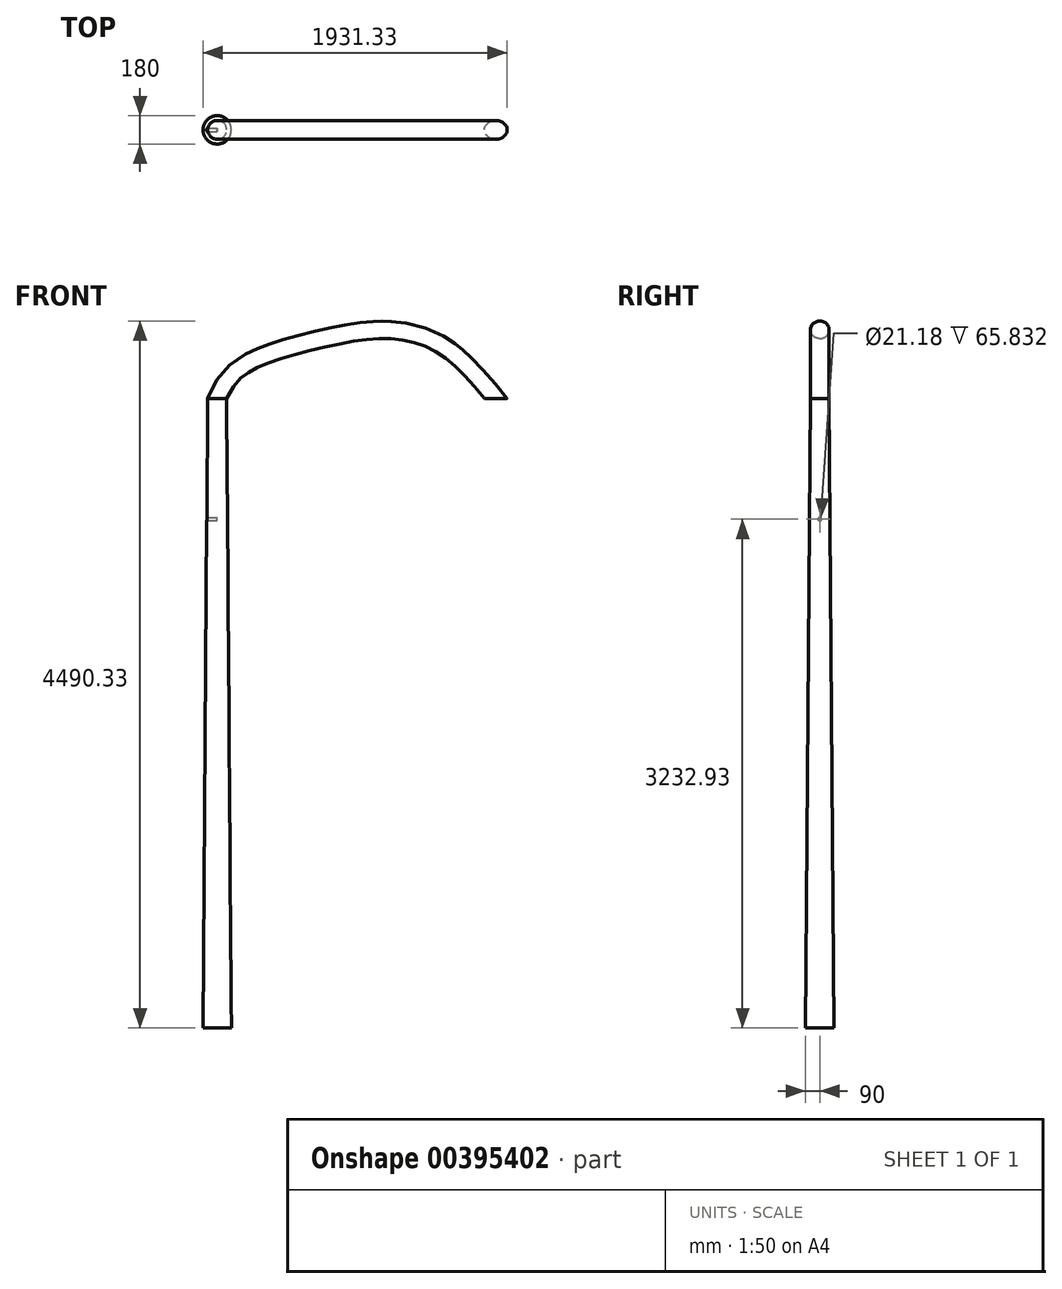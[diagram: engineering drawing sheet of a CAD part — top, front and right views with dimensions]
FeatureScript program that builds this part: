
annotation { "Feature Type Name" : "Feature", "Feature Type Description" : "" }
export const myFeature = defineFeature(function(context is Context, id is Id, definition is map)
    precondition{}
    {
        {
            var Q0;
            Q0=qCreatedBy(makeId("Top.planeOp"),FACE);
            var sketch = newSketch(context, id + "F0", { "sketchPlane" : qUnion([Q0])});
            skCircle(sketch, "E0", {"center": v(0, 0) * mm, "radius": 60 * mm});
            skSolve(sketch);
        }
        {
            var Q0;
            Q0=qCreatedBy(makeId("Top.planeOp"),FACE);
            cPlane(context, id + "F1", {"entities" : qUnion([Q0]), "cplaneType" : CPlaneType.OFFSET, "offset" : 4000 * mm, "oppositeDirection" : true, "width" : 150 * mm, "height" : 150 * mm});
        }
        {
            var Q0;
            Q0=qCreatedBy(id+"F1.planeOp",FACE);
            var sketch = newSketch(context, id + "F2", { "sketchPlane" : qUnion([Q0])});
            skCircle(sketch, "E1", {"center": v(0, 0) * mm, "radius": 90 * mm});
            skSolve(sketch);
        }
        {
            var Q0;
            Q0=makeQuery(id+"F0.imprint","IMPRINT",FACE,{"disambiguationData":[TD([[makeQuery(id+"F0.imprint","IMPRINT",EDGE,{"derivedFrom":sQuery(id+"F0.wireOp",EDGE,"E0")}),1.0]])]});
            var Q1;
            Q1=makeQuery(id+"F2.imprint","IMPRINT",FACE,{"disambiguationData":[TD([[makeQuery(id+"F2.imprint","IMPRINT",EDGE,{"derivedFrom":sQuery(id+"F2.wireOp",EDGE,"E1")}),1.0]])]});
            loft(context, id + "F3", {"sheetProfilesArray" : [{ "sheetProfileEntities" : qUnion([Q0]) }, { "sheetProfileEntities" : qUnion([Q1]) }]});
        }
        {
            var Q0;
            Q0=qCreatedBy(makeId("Right.planeOp"),FACE);
            cPlane(context, id + "F4", {"entities" : qUnion([Q0]), "cplaneType" : CPlaneType.OFFSET, "offset" : 1100 * mm, "width" : 150 * mm, "height" : 150 * mm});
        }
        {
            var Q0;
            Q0=qCreatedBy(id+"F4.planeOp",FACE);
            var sketch = newSketch(context, id + "F5", { "sketchPlane" : qUnion([Q0])});
            skCircle(sketch, "E2", {"center": v(0, 405) * mm, "radius": 84.19 * mm});
            skSolve(sketch);
        }
        {
            var Q0;
            Q0=qCreatedBy(makeId("Top.planeOp"),FACE);
            var sketch = newSketch(context, id + "F6", { "sketchPlane" : qUnion([Q0])});
            skCircle(sketch, "E3", {"center": v(1778.5, 0) * mm, "radius": 62.82 * mm});
            skSolve(sketch);
        }
        {
            var Q0;
            Q0=qCreatedBy(makeId("Front.planeOp"),FACE);
            var sketch = newSketch(context, id + "F7", { "sketchPlane" : qUnion([Q0])});
            skLineSegment(sketch, "E4.0", {"start": v(1100, 489.2) * mm, "end": v(1100, 320.82) * mm});
            skLineSegment(sketch, "E5.0", {"start": v(60, 0) * mm, "end": v(-60, 0) * mm});
            skLineSegment(sketch, "E6", {"start": v(1100, 405) * mm, "end": v(1100, 489.2) * mm});
            skLineSegment(sketch, "E7", {"start": v(30, 0) * mm, "end": v(-60, 0) * mm});
            skLineSegment(sketch, "E8.0", {"start": v(1715.69, 0) * mm, "end": v(1841.33, 0) * mm});
            skFitSpline(sketch, "E9", {"points": [v(-60, 0) * mm, v(204.15, 292.84) * mm, v(690.76, 441.3) * mm, v(1100, 489.2) * mm, v(1475.98, 372.42) * mm, v(1841.33, 0) * mm], "startDerivative": vector(1008.1, 2538.37) * mm, "endDerivative": vector(1607.03, -1968.32) * mm});
            skFitSpline(sketch, "E10", {"points": [v(204.15, 292.84) * mm, v(248.1, 313) * mm], "startDerivative": vector(43.73, 21.04) * mm, "endDerivative": vector(43.73, 21.04) * mm});
            skSolve(sketch);
        }
        {
            var Q0;
            Q0=makeQuery(id+"F3.opLoft","CAP_FACE",FACE,{"disambiguationData":[OSD([makeQuery(id+"F0.imprint","IMPRINT",FACE,{"disambiguationData":[TD([[makeQuery(id+"F0.imprint","IMPRINT",EDGE,{"derivedFrom":sQuery(id+"F0.wireOp",EDGE,"E0")}),1.0]])]})])],"isStart":true});
            var Q1;
            Q1=sQuery(id+"F7.wireOp",EDGE,"E9");
            sweep(context, id + "F8", {"operationType" : NewBodyOperationType.ADD, "profiles" : qUnion([Q0]), "path" : qUnion([Q1])});
        }
        {
            var Q0;
            Q0=qCreatedBy(makeId("Top.planeOp"),FACE);
            var sketch = newSketch(context, id + "F9", { "sketchPlane" : qUnion([Q0])});
            skCircle(sketch, "E11", {"center": v(1785.5, 0) * mm, "radius": 217.67 * mm});
            skSolve(sketch);
        }
        {
            var Q0;
            Q0 = qSketchRegion(id + "F9", true);
            extrude(context, id + "F10", {"entities" : qUnion([Q0]), "operationType" : NewBodyOperationType.REMOVE, "oppositeDirection" : true, "depth" : 250 * mm});
        }
        {
            var Q0;
            Q0=qCreatedBy(makeId("Right.planeOp"),FACE);
            var sketch = newSketch(context, id + "F11", { "sketchPlane" : qUnion([Q0])});
            skCircle(sketch, "E12", {"center": v(0, -767.07) * mm, "radius": 10.59 * mm});
            skSolve(sketch);
        }
        {
            var Q0;
            Q0 = qSketchRegion(id + "F11", true);
            extrude(context, id + "F12", {"entities" : qUnion([Q0]), "operationType" : NewBodyOperationType.REMOVE, "endBound" : BoundingType.THROUGH_ALL, "oppositeDirection" : true, "depth" : 25 * mm});
        }
    });
